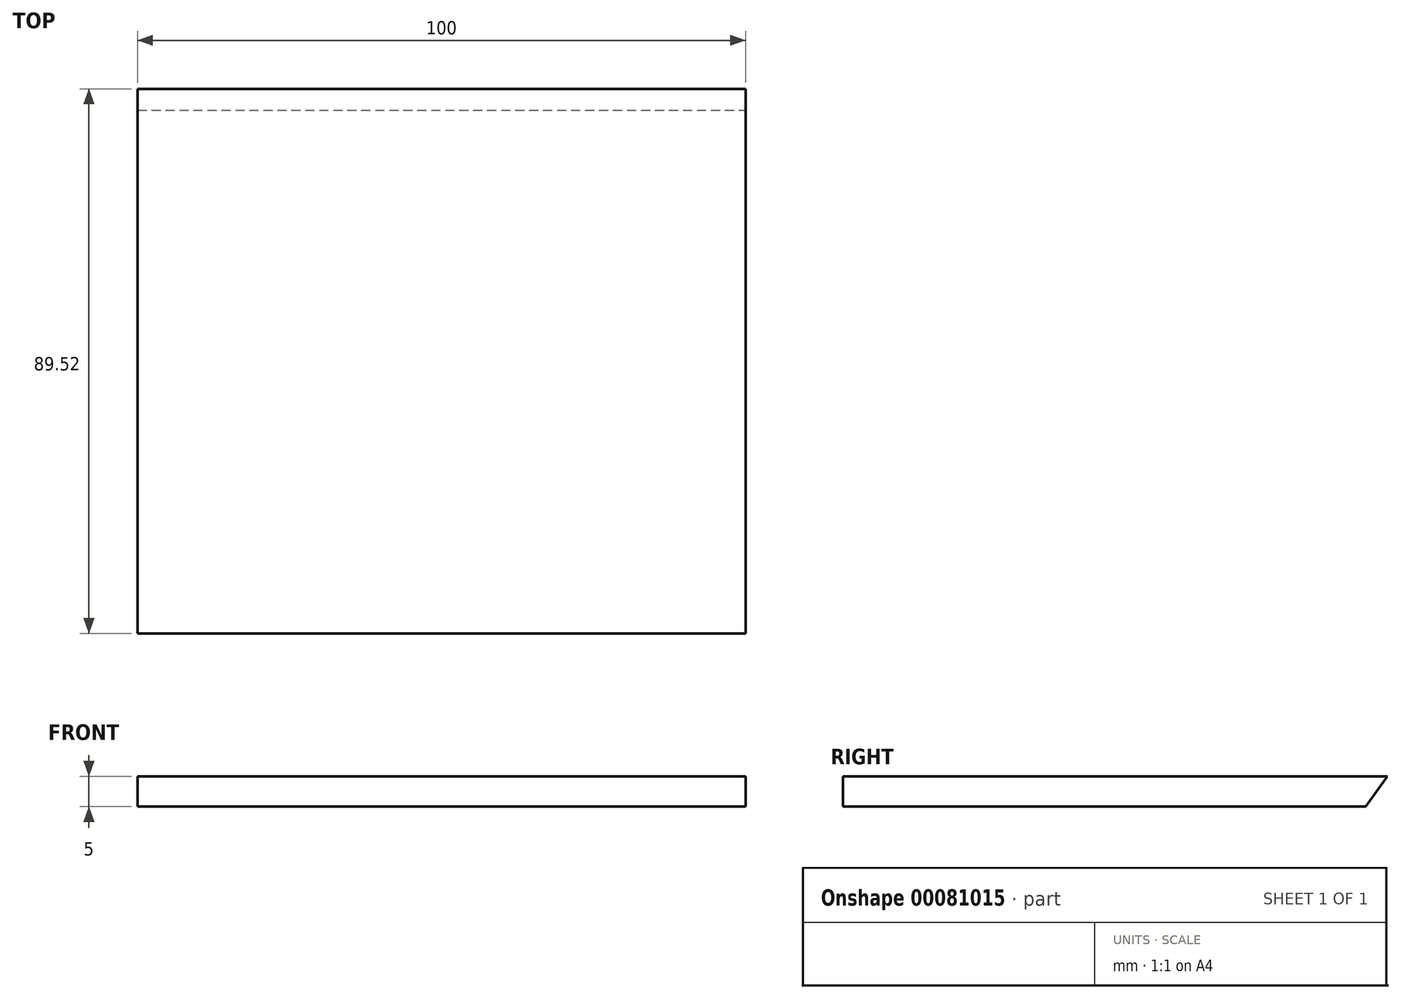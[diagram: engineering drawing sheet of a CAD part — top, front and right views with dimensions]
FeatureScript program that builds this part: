
annotation { "Feature Type Name" : "Feature", "Feature Type Description" : "" }
export const myFeature = defineFeature(function(context is Context, id is Id, definition is map)
    precondition{}
    {
        {
            var Q0;
            Q0=qCreatedBy(makeId("Top.planeOp"),FACE);
            var sketch = newSketch(context, id + "F0", { "sketchPlane" : qUnion([Q0])});
            skLineSegment(sketch, "E0.bottom", {"start": v(-100, 91.02) * mm, "end": v(0, 91.02) * mm});
            skLineSegment(sketch, "E0.top", {"start": v(-100, 0) * mm, "end": v(0, 0) * mm});
            skLineSegment(sketch, "E0.left", {"start": v(-100, 91.02) * mm, "end": v(-100, 0) * mm});
            skLineSegment(sketch, "E0.right", {"start": v(0, 91.02) * mm, "end": v(0, 0) * mm});
            skPoint(sketch, "E1", {"position": v(-100, 41.02) * mm});
            skSolve(sketch);
        }
        {
            var Q0;
            Q0 = qSketchRegion(id + "F0", true);
            extrude(context, id + "F1", {"entities" : qUnion([Q0]), "endBound" : BoundingType.SYMMETRIC, "depth" : 5 * mm});
        }
        {
            var Q0;
            Q0=makeQuery(id+"F1.opExtrude","CAP_EDGE",EDGE,{"disambiguationData":[OSD([sQuery(id+"F0.wireOp",EDGE,"E0.bottom")])],"isStart":true});
            chamfer(context, id + "F2", {"entities" : qUnion([Q0]), "chamferType" : ChamferType.OFFSET_ANGLE, "width" : 5 * mm, "oppositeDirection" : false, "angle" : 55 * degree, "tangentPropagation" : true});
        }
    });
